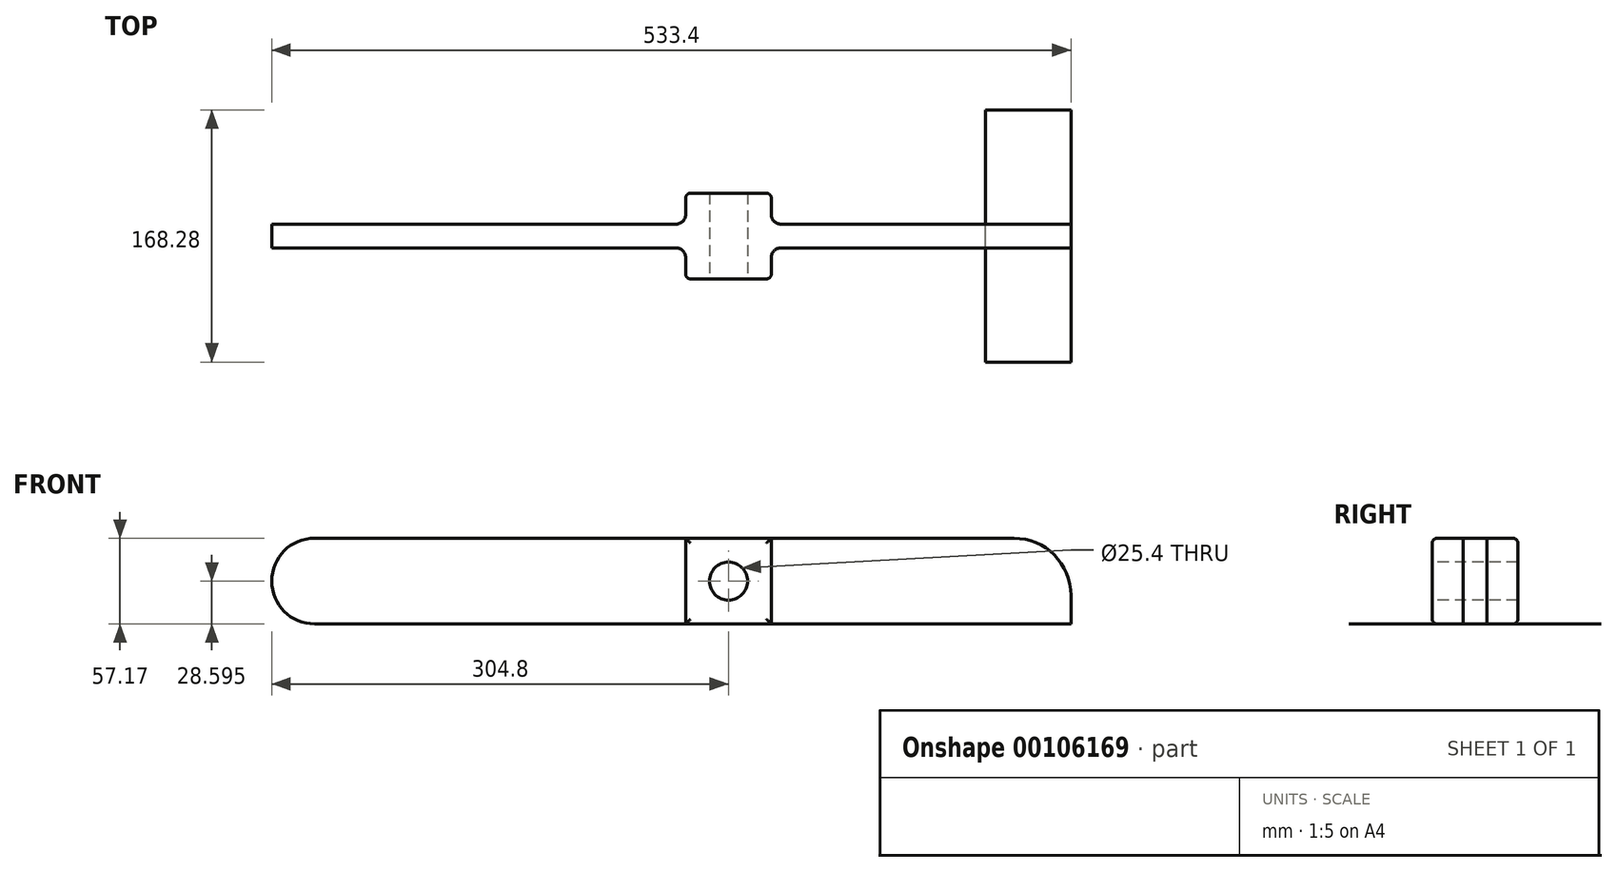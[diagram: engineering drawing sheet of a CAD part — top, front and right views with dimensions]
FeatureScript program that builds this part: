
annotation { "Feature Type Name" : "Feature", "Feature Type Description" : "" }
export const myFeature = defineFeature(function(context is Context, id is Id, definition is map)
    precondition{}
    {
        {
            var Q0;
            Q0=qCreatedBy(makeId("Top.planeOp"),FACE);
            var sketch = newSketch(context, id + "F0", { "sketchPlane" : qUnion([Q0])});
            skLineSegment(sketch, "E0", {"start": v(34.92, 0) * mm, "end": v(228.6, 0) * mm});
            skLineSegment(sketch, "E1", {"start": v(-34.93, 0) * mm, "end": v(-304.8, 0) * mm});
            skLineSegment(sketch, "E2.0", {"start": v(34.92, 15.88) * mm, "end": v(228.6, 15.88) * mm});
            skLineSegment(sketch, "E3.0", {"start": v(-34.93, 15.88) * mm, "end": v(-304.8, 15.87) * mm});
            skLineSegment(sketch, "E4", {"start": v(-304.8, 15.87) * mm, "end": v(-304.8, 0) * mm});
            skLineSegment(sketch, "E5.0", {"start": v(0, -20.64) * mm, "end": v(28.58, -20.64) * mm});
            skLineSegment(sketch, "E6.0", {"start": v(0, 36.51) * mm, "end": v(28.58, 36.51) * mm});
            skLineSegment(sketch, "E7.0", {"start": v(-28.58, 36.51) * mm, "end": v(-28.58, 22.23) * mm});
            skLineSegment(sketch, "E8.0", {"start": v(28.58, 36.51) * mm, "end": v(28.58, 22.23) * mm});
            skLineSegment(sketch, "E9", {"start": v(-28.58, 36.51) * mm, "end": v(0, 36.51) * mm});
            skLineSegment(sketch, "E10", {"start": v(-28.58, -20.64) * mm, "end": v(0, -20.64) * mm});
            skLineSegment(sketch, "E11.trimOffspring", {"start": v(28.58, -6.35) * mm, "end": v(28.58, -20.64) * mm});
            skLineSegment(sketch, "E12.trimOffspring", {"start": v(-28.58, -6.35) * mm, "end": v(-28.58, -20.64) * mm});
            skPoint(sketch, "E13.visualSharp", {"position": v(28.58, 0) * mm});
            skArc(sketch, "E13.filletArc", {"start": v(34.92, 0) * mm, "mid": v(30.43, -1.86) * mm, "end": v(28.58, -6.35) * mm});
            skPoint(sketch, "E14.visualSharp", {"position": v(28.58, 15.88) * mm});
            skArc(sketch, "E14.filletArc", {"start": v(28.58, 22.23) * mm, "mid": v(30.43, 17.73) * mm, "end": v(34.92, 15.87) * mm});
            skPoint(sketch, "E15.visualSharp", {"position": v(-28.58, 15.88) * mm});
            skArc(sketch, "E15.filletArc", {"start": v(-34.93, 15.88) * mm, "mid": v(-30.43, 17.73) * mm, "end": v(-28.58, 22.23) * mm});
            skPoint(sketch, "E16.visualSharp", {"position": v(-28.58, 0) * mm});
            skArc(sketch, "E16.filletArc", {"start": v(-28.57, -6.35) * mm, "mid": v(-30.43, -1.86) * mm, "end": v(-34.93, 0) * mm});
            skLineSegment(sketch, "E17.0", {"start": v(228.6, 15.88) * mm, "end": v(228.6, 0) * mm});
            skSolve(sketch);
        }
        {
            var Q0;
            Q0=makeQuery(id+"F0.imprint","IMPRINT",FACE,{"disambiguationData":[TD([[makeQuery(id+"F0.imprint","IMPRINT",EDGE,{"derivedFrom":sQuery(id+"F0.wireOp",EDGE,"E0")}),1.0]])]});
            extrude(context, id + "F1", {"entities" : qUnion([Q0]), "depth" : 57.15 * mm});
        }
        {
            var Q0;
            Q0=makeQuery(id+"F1.opExtrude","SWEPT_FACE",FACE,{"disambiguationData":[OSD([sQuery(id+"F0.wireOp",EDGE,"E6.0"),sQuery(id+"F0.wireOp",EDGE,"E9")])]});
            var Q1;
            Q1=makeQuery(id+"F1.opExtrude","SWEPT_FACE",FACE,{"disambiguationData":[OSD([sQuery(id+"F0.wireOp",EDGE,"E5.0"),sQuery(id+"F0.wireOp",EDGE,"E10")])]});
            fillet(context, id + "F2", {"entities" : qUnion([Q0, Q1]), "radius" : 3.17 * mm, "tangentPropagation" : true, "allowEdgeOverflow" : false});
        }
        {
            var Q0;
            Q0=makeQuery(id+"F1.opExtrude","CAP_EDGE",EDGE,{"disambiguationData":[OSD([sQuery(id+"F0.wireOp",EDGE,"E4")])],"isStart":false});
            var Q1;
            Q1=makeQuery(id+"F1.opExtrude","CAP_EDGE",EDGE,{"disambiguationData":[OSD([sQuery(id+"F0.wireOp",EDGE,"E4")])],"isStart":true});
            fillet(context, id + "F3", {"entities" : qUnion([Q0, Q1]), "radius" : 28.57 * mm, "tangentPropagation" : true, "allowEdgeOverflow" : false});
        }
        {
            var Q0;
            Q0=qCreatedBy(makeId("Front.planeOp"),FACE);
            var sketch = newSketch(context, id + "F4", { "sketchPlane" : qUnion([Q0])});
            skLineSegment(sketch, "E18", {"start": v(0, 0) * mm, "end": v(0, 57.15) * mm});
            skCircle(sketch, "E19", {"center": v(0, 28.58) * mm, "radius": 12.7 * mm});
            skLineSegment(sketch, "E20", {"start": v(0, 28.58) * mm, "end": v(-215.9, 28.58) * mm});
            skSolve(sketch);
        }
        {
            var Q0;
            Q0=sQuery(id+"F4.wireOp",VERTEX,"E19.center");
            var Q1;
            Q1=makeQuery(id+"F1.opExtrude","SWEPT_BODY",BODY,{"disambiguationData":[OSD([sQuery(id+"F0.wireOp",EDGE,"E0"),sQuery(id+"F0.wireOp",EDGE,"E1"),sQuery(id+"F0.wireOp",EDGE,"E2.0"),sQuery(id+"F0.wireOp",EDGE,"E3.0"),sQuery(id+"F0.wireOp",EDGE,"E4"),sQuery(id+"F0.wireOp",EDGE,"91bae051-fccf-4571-8f7a-4858285b8110"),sQuery(id+"F0.wireOp",EDGE,"E5.0"),sQuery(id+"F0.wireOp",EDGE,"E6.0"),sQuery(id+"F0.wireOp",EDGE,"E7.0"),sQuery(id+"F0.wireOp",EDGE,"E8.0"),sQuery(id+"F0.wireOp",EDGE,"E9"),sQuery(id+"F0.wireOp",EDGE,"E10"),sQuery(id+"F0.wireOp",EDGE,"E11.trimOffspring"),sQuery(id+"F0.wireOp",EDGE,"E12.trimOffspring"),sQuery(id+"F0.wireOp",EDGE,"E13.filletArc"),sQuery(id+"F0.wireOp",EDGE,"E14.filletArc"),sQuery(id+"F0.wireOp",EDGE,"E15.filletArc"),sQuery(id+"F0.wireOp",EDGE,"E16.filletArc")])]});
            hole(context, id + "F5", {"style" : HoleStyle.SIMPLE, "holeDiameter" : 25.4 * mm, "endStyle" : HoleEndStyle.BLIND, "holeDepth" : 38.1 * mm, "locations" : qUnion([Q0]), "scope" : qUnion([Q1])});
        }
        {
            var Q0;
            Q0=sQuery(id+"F4.wireOp",VERTEX,"E19.center");
            var Q1;
            Q1=makeQuery(id+"F1.opExtrude","SWEPT_BODY",BODY,{"disambiguationData":[OSD([sQuery(id+"F0.wireOp",EDGE,"E0"),sQuery(id+"F0.wireOp",EDGE,"E1"),sQuery(id+"F0.wireOp",EDGE,"E2.0"),sQuery(id+"F0.wireOp",EDGE,"E3.0"),sQuery(id+"F0.wireOp",EDGE,"E4"),sQuery(id+"F0.wireOp",EDGE,"91bae051-fccf-4571-8f7a-4858285b8110"),sQuery(id+"F0.wireOp",EDGE,"E5.0"),sQuery(id+"F0.wireOp",EDGE,"E6.0"),sQuery(id+"F0.wireOp",EDGE,"E7.0"),sQuery(id+"F0.wireOp",EDGE,"E8.0"),sQuery(id+"F0.wireOp",EDGE,"E9"),sQuery(id+"F0.wireOp",EDGE,"E10"),sQuery(id+"F0.wireOp",EDGE,"E11.trimOffspring"),sQuery(id+"F0.wireOp",EDGE,"E12.trimOffspring"),sQuery(id+"F0.wireOp",EDGE,"E13.filletArc"),sQuery(id+"F0.wireOp",EDGE,"E14.filletArc"),sQuery(id+"F0.wireOp",EDGE,"E15.filletArc"),sQuery(id+"F0.wireOp",EDGE,"E16.filletArc")])]});
            hole(context, id + "F6", {"style" : HoleStyle.SIMPLE, "holeDiameter" : 25.4 * mm, "endStyle" : HoleEndStyle.THROUGH, "oppositeDirection" : true, "locations" : qUnion([Q0]), "scope" : qUnion([Q1])});
        }
        {
            var Q0;
            Q0=makeQuery(id+"F1.opExtrude","CAP_EDGE",EDGE,{"disambiguationData":[OSD([sQuery(id+"F0.wireOp",EDGE,"E17.0")])],"isStart":false});
            fillet(context, id + "F7", {"entities" : qUnion([Q0]), "radius" : 38.1 * mm, "tangentPropagation" : true, "allowEdgeOverflow" : false});
        }
        {
            var Q0;
            Q0=qCreatedBy(makeId("Top.planeOp"),FACE);
            var sketch = newSketch(context, id + "F8", { "sketchPlane" : qUnion([Q0])});
            skLineSegment(sketch, "E21", {"start": v(228.6, 0) * mm, "end": v(228.6, -76.2) * mm});
            skLineSegment(sketch, "E22.bottom", {"start": v(228.6, -76.2) * mm, "end": v(171.45, -76.2) * mm});
            skLineSegment(sketch, "E22.top", {"start": v(228.6, 92.08) * mm, "end": v(171.45, 92.08) * mm});
            skLineSegment(sketch, "E22.left", {"start": v(228.6, -76.2) * mm, "end": v(228.6, 92.08) * mm});
            skLineSegment(sketch, "E22.right", {"start": v(171.45, -76.2) * mm, "end": v(171.45, 92.08) * mm});
            skSolve(sketch);
        }
        {
            var Q0;
            {var subQ0=sQuery(id+"F8.wireOp",EDGE,"E22.bottom");Q0=makeQuery(id+"F8.imprint","IMPRINT",FACE,{"disambiguationData":[TD([[makeQuery(id+"F8.imprint","IMPRINT",EDGE,{"derivedFrom":subQ0}),-1.0]])]});}
            extrude(context, id + "F9", {"entities" : qUnion([Q0]), "operationType" : NewBodyOperationType.ADD, "oppositeDirection" : true, "depth" : 5 / 203.2 * mm});
        }
    });
